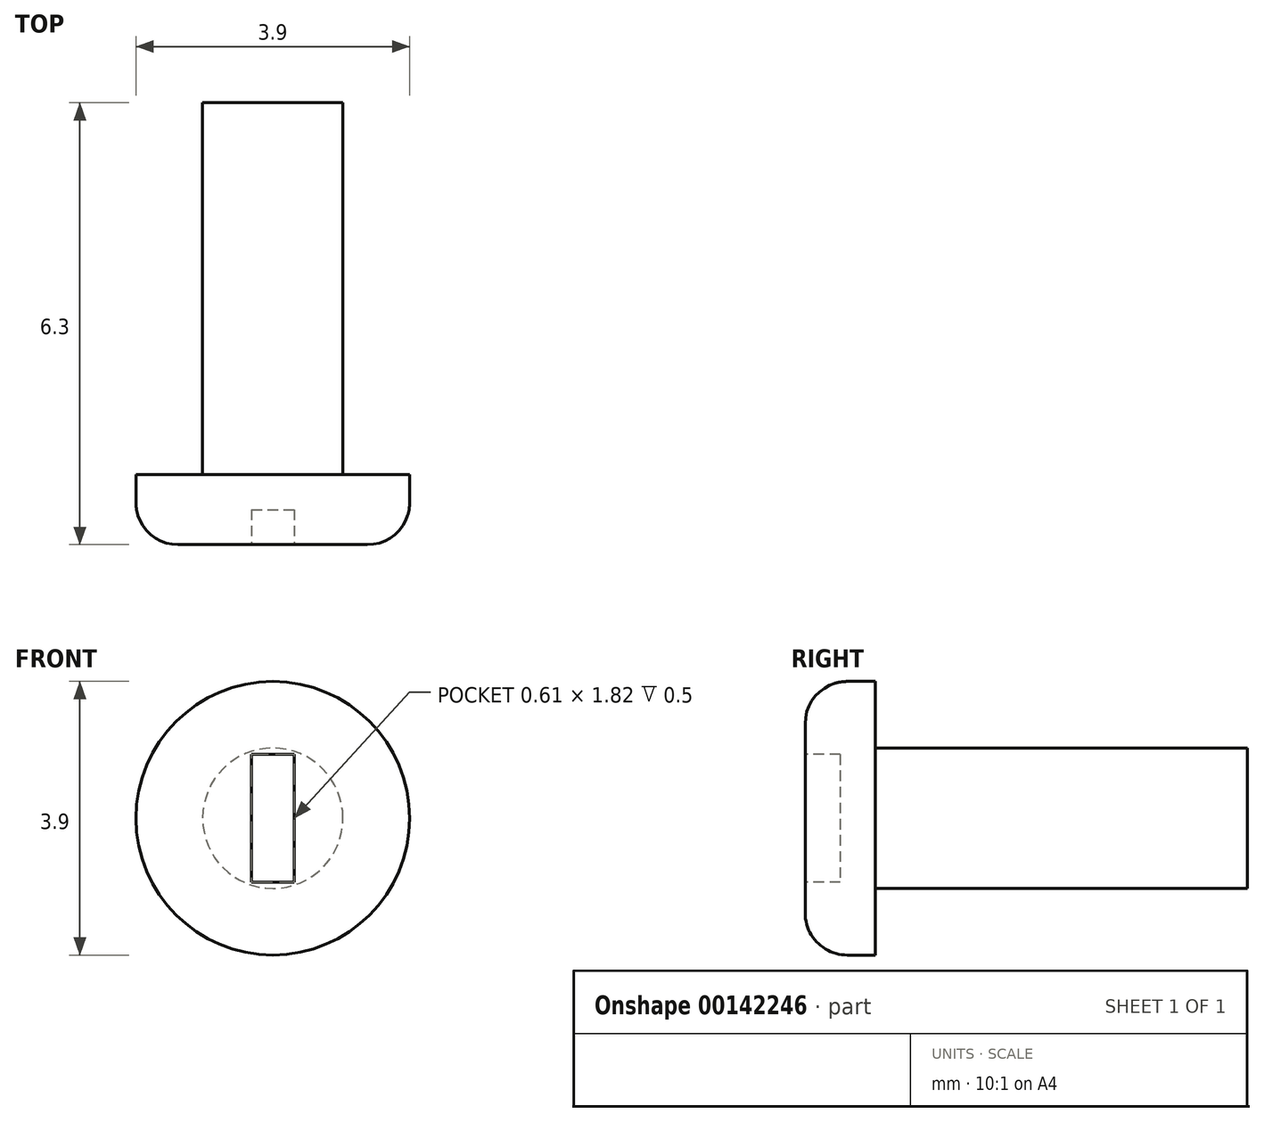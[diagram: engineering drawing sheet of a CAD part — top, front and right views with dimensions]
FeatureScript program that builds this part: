
annotation { "Feature Type Name" : "Feature", "Feature Type Description" : "" }
export const myFeature = defineFeature(function(context is Context, id is Id, definition is map)
    precondition{}
    {
        {
            var Q0;
            Q0=qCreatedBy(makeId("Front.planeOp"),FACE);
            var sketch = newSketch(context, id + "F0", { "sketchPlane" : qUnion([Q0])});
            skCircle(sketch, "E0", {"center": v(0, 0) * mm, "radius": 1 * mm});
            skSolve(sketch);
        }
        {
            var Q0;
            Q0=makeQuery(id+"F0.imprint","IMPRINT",FACE,{"disambiguationData":[TD([[makeQuery(id+"F0.imprint","IMPRINT",EDGE,{"derivedFrom":sQuery(id+"F0.wireOp",EDGE,"E0")}),1.0]])]});
            extrude(context, id + "F1", {"entities" : qUnion([Q0]), "depth" : 5.3 * mm});
        }
        {
            var Q0;
            Q0=makeQuery(id+"F1.opExtrude","CAP_FACE",FACE,{"disambiguationData":[OSD([sQuery(id+"F0.wireOp",EDGE,"E0")])],"isStart":false});
            cPlane(context, id + "F2", {"entities" : qUnion([Q0]), "cplaneType" : CPlaneType.OFFSET, "offset" : 0 * mm, "width" : 150 * mm, "height" : 150 * mm});
        }
        {
            var Q0;
            Q0=qCreatedBy(id+"F2.planeOp",FACE);
            var sketch = newSketch(context, id + "F3", { "sketchPlane" : qUnion([Q0])});
            skCircle(sketch, "E1", {"center": v(0, 0) * mm, "radius": 1.95 * mm});
            skSolve(sketch);
        }
        {
            var Q0;
            Q0=makeQuery(id+"F3.imprint","IMPRINT",FACE,{"disambiguationData":[TD([[makeQuery(id+"F3.imprint","IMPRINT",EDGE,{"derivedFrom":sQuery(id+"F3.wireOp",EDGE,"E1")}),1.0]])]});
            extrude(context, id + "F4", {"entities" : qUnion([Q0]), "depth" : 1 * mm});
        }
        {
            var Q0;
            Q0=makeQuery(id+"F4.opExtrude","CAP_FACE",FACE,{"disambiguationData":[OSD([sQuery(id+"F3.wireOp",EDGE,"E1")])],"isStart":false});
            cPlane(context, id + "F5", {"entities" : qUnion([Q0]), "cplaneType" : CPlaneType.OFFSET, "offset" : 0 * mm, "width" : 150 * mm, "height" : 150 * mm});
        }
        {
            var Q0;
            Q0=qCreatedBy(id+"F5.planeOp",FACE);
            var sketch = newSketch(context, id + "F6", { "sketchPlane" : qUnion([Q0])});
            skLineSegment(sketch, "E2", {"start": v(-0.3, -0.91) * mm, "end": v(0.3, -0.91) * mm});
            skLineSegment(sketch, "E3", {"start": v(0.3, -0.91) * mm, "end": v(0.3, 0.91) * mm});
            skLineSegment(sketch, "E4", {"start": v(0.3, 0.91) * mm, "end": v(-0.3, 0.91) * mm});
            skLineSegment(sketch, "E5", {"start": v(-0.3, 0.91) * mm, "end": v(-0.3, -0.91) * mm});
            skSolve(sketch);
        }
        {
            var Q0;
            Q0=makeQuery(id+"F6.imprint","IMPRINT",FACE,{"disambiguationData":[TD([[makeQuery(id+"F6.imprint","IMPRINT",EDGE,{"derivedFrom":sQuery(id+"F6.wireOp",EDGE,"E2")}),1.0]])]});
            extrude(context, id + "F7", {"entities" : qUnion([Q0]), "operationType" : NewBodyOperationType.REMOVE, "oppositeDirection" : true, "depth" : 0.5 * mm});
        }
        {
            var Q0;
            Q0=makeQuery(id+"F4.opExtrude","CAP_EDGE",EDGE,{"disambiguationData":[OSD([sQuery(id+"F3.wireOp",EDGE,"E1")])],"isStart":false});
            fillet(context, id + "F8", {"entities" : qUnion([Q0]), "radius" : 0.6 * mm, "tangentPropagation" : true, "allowEdgeOverflow" : false});
        }
    });
